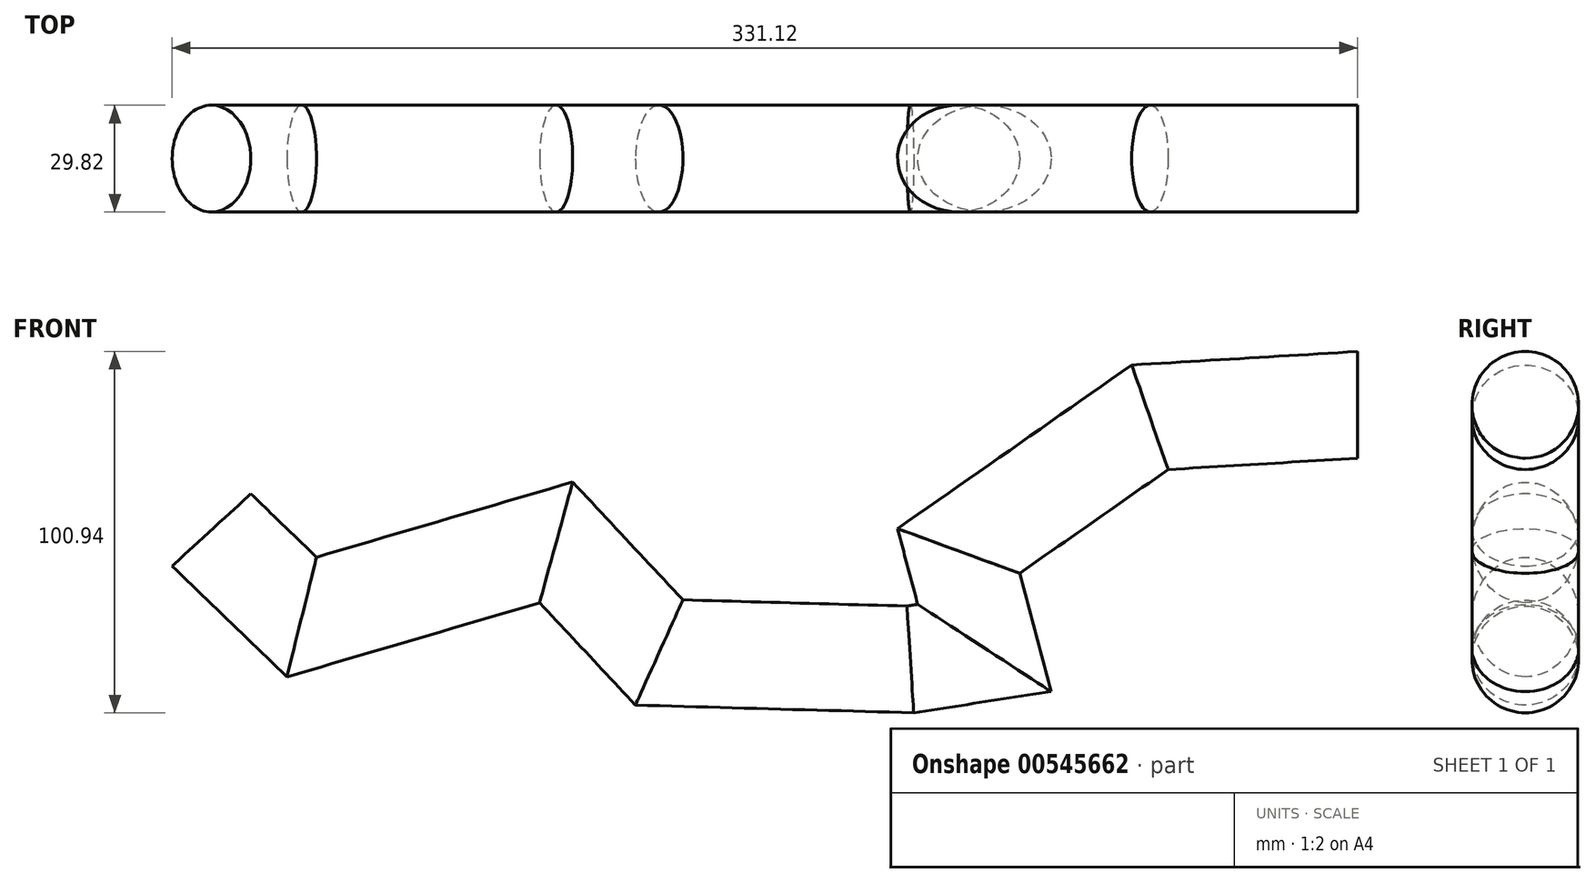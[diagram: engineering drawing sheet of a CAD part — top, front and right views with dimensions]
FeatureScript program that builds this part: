
annotation { "Feature Type Name" : "Feature", "Feature Type Description" : "" }
export const myFeature = defineFeature(function(context is Context, id is Id, definition is map)
    precondition{}
    {
        {
            var Q0;
            Q0=qCreatedBy(makeId("Right.planeOp"),FACE);
            var sketch = newSketch(context, id + "F0", { "sketchPlane" : qUnion([Q0])});
            skCircle(sketch, "E0", {"center": v(-14.48, 56.17) * mm, "radius": 14.9 * mm});
            skSolve(sketch);
        }
        {
            var Q0;
            Q0=qCreatedBy(makeId("Front.planeOp"),FACE);
            var sketch = newSketch(context, id + "F1", { "sketchPlane" : qUnion([Q0])});
            skLineSegment(sketch, "E1", {"start": v(20.87, 40.63) * mm, "end": v(-31.37, 37.5) * mm});
            skLineSegment(sketch, "E2", {"start": v(-31.37, 37.5) * mm, "end": v(-71.34, 9.57) * mm});
            skLineSegment(sketch, "E3", {"start": v(-71.34, 9.57) * mm, "end": v(-62.36, -24.2) * mm});
            skLineSegment(sketch, "E4", {"start": v(-62.36, -24.2) * mm, "end": v(-102.98, -30.5) * mm});
            skLineSegment(sketch, "E5", {"start": v(-102.98, -30.5) * mm, "end": v(-181.68, -28.34) * mm});
            skLineSegment(sketch, "E6", {"start": v(-181.68, -28.34) * mm, "end": v(-208.16, 0) * mm});
            skLineSegment(sketch, "E7", {"start": v(-208.16, 0) * mm, "end": v(-278.7, -20.68) * mm});
            skLineSegment(sketch, "E8", {"start": v(-278.7, -20.68) * mm, "end": v(-311.64, 11.13) * mm});
            skSolve(sketch);
        }
        {
            var Q0;
            Q0 = qSketchRegion(id + "F0", true);
            var Q1;
            Q1 = qConstructionFilter(qBodyType(qCreatedBy(id + "F1" ,EDGE), BodyType.WIRE), ConstructionObject.NO);
            sweep(context, id + "F2", {"profiles" : qUnion([Q0]), "path" : qUnion([Q1])});
        }
    });
